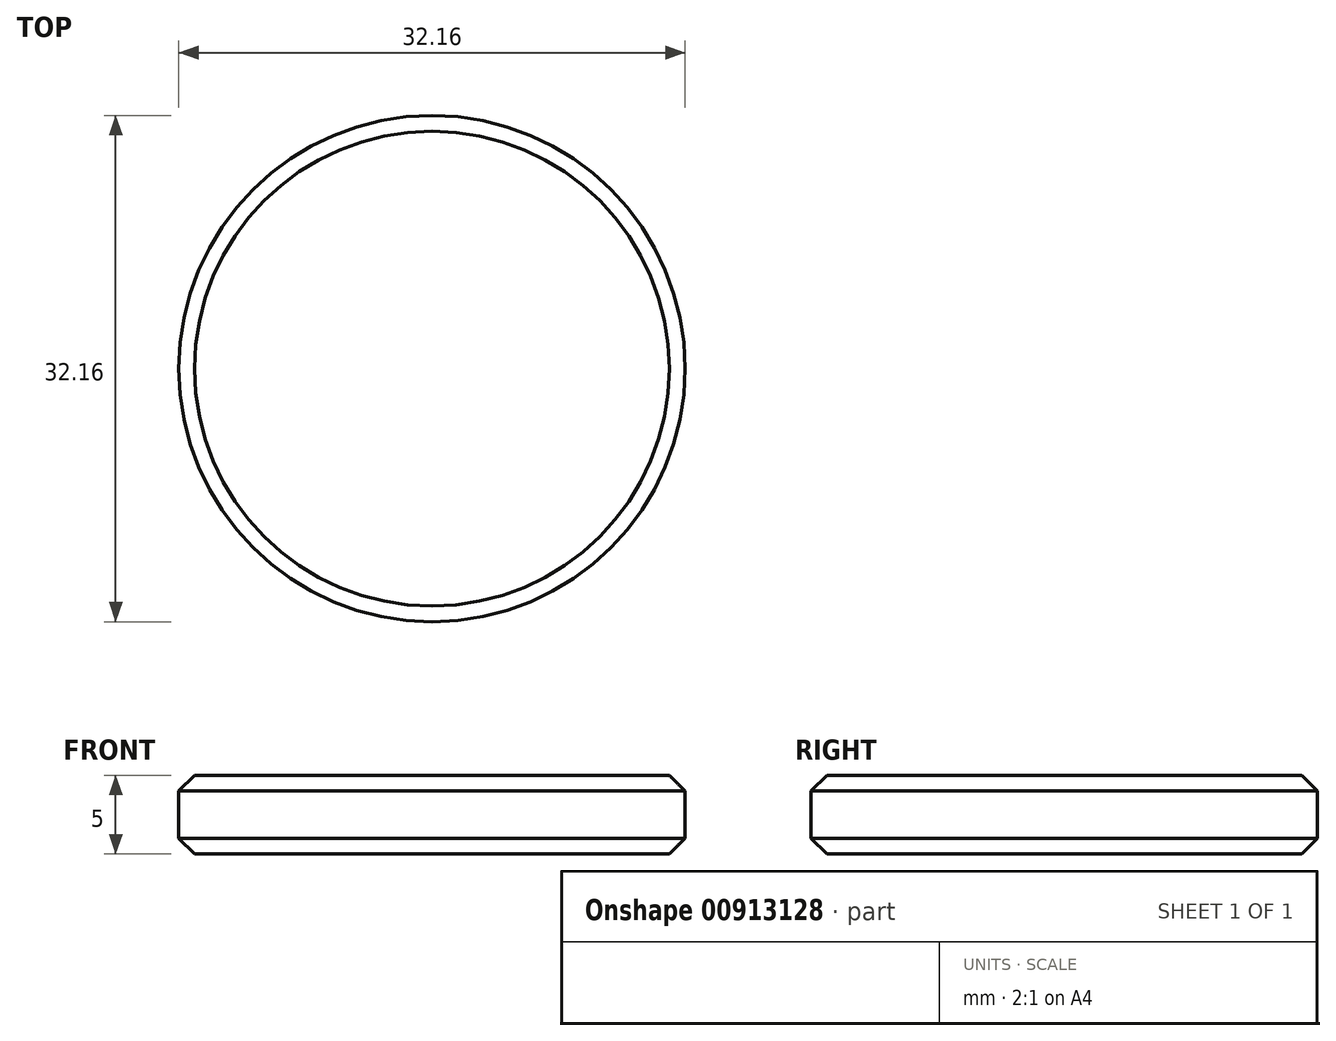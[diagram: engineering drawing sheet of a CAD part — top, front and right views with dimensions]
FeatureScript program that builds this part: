
annotation { "Feature Type Name" : "Feature", "Feature Type Description" : "" }
export const myFeature = defineFeature(function(context is Context, id is Id, definition is map)
    precondition{}
    {
        {
            var Q0;
            Q0=qCreatedBy(makeId("Top.planeOp"),FACE);
            var sketch = newSketch(context, id + "F0", { "sketchPlane" : qUnion([Q0])});
            skCircle(sketch, "E0", {"center": v(0, 0) * mm, "radius": 16.08 * mm});
            skSolve(sketch);
        }
        {
            var Q0;
            Q0=makeQuery(id+"F0.imprint","IMPRINT",FACE,{"disambiguationData":[TD([[makeQuery(id+"F0.imprint","IMPRINT",EDGE,{"derivedFrom":sQuery(id+"F0.wireOp",EDGE,"E0")}),1.0]])]});
            extrude(context, id + "F1", {"entities" : qUnion([Q0]), "depth" : 5 * mm, "offsetDistance" : 25 * mm});
        }
        {
            var Q0;
            Q0=makeQuery(id+"F1.opExtrude","CAP_EDGE",EDGE,{"disambiguationData":[OSD([sQuery(id+"F0.wireOp",EDGE,"E0")])],"isStart":false});
            chamfer(context, id + "F2", {"entities" : qUnion([Q0]), "width" : 1 * mm, "tangentPropagation" : true});
        }
        {
            var Q0;
            Q0=qCreatedBy(makeId("Top.planeOp"),FACE);
            var sketch = newSketch(context, id + "F3", { "sketchPlane" : qUnion([Q0])});
            skCircle(sketch, "E1", {"center": v(0, 0) * mm, "radius": 6 * mm});
            skSolve(sketch);
        }
        {
            var Q0;
            Q0=sQuery(id+"F3.wireOp",EDGE,"E1");
            extrude(context, id + "F4", {"bodyType" : ToolBodyType.SURFACE, "surfaceEntities" : qUnion([Q0]), "oppositeDirection" : true, "depth" : 50 * mm, "offsetDistance" : 25 * mm});
        }
        {
            var Q0;
            Q0=makeQuery(id+"F1.opExtrude","CAP_EDGE",EDGE,{"disambiguationData":[OSD([sQuery(id+"F0.wireOp",EDGE,"E0")])],"isStart":true});
            chamfer(context, id + "F5", {"entities" : qUnion([Q0]), "width" : 1 * mm, "tangentPropagation" : true});
        }
    });
